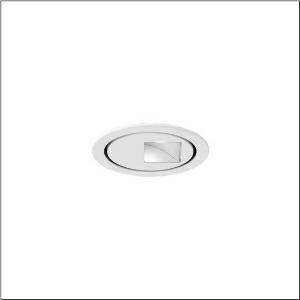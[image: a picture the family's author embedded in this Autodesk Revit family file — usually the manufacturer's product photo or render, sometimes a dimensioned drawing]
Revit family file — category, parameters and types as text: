
# Revit family: lunis_11_micro_round_51dj11b71wm21
name_source: partatom
category: Lighting Fixtures
units: mm (PartAtom-declared; Revit-internal decimal feet)

## family parameters
Cut with Voids When Loaded = No
Host = Face
Light Source = No
Part Type = Normal
Room Calculation Point = No
Round Connector Dimension = Use Diameter
Shared = No

## types (1)
- Lunis 11 micro round (1 x LED 3000K / CRI = 90 (unbekannt), 1100 lm, 3000K)
    Apparent Load = 20 VA
    CIE Flux Codes = 42 75 96 100 100
    Color Rendering = 90
    Color Temperature = 3000K
    Default Elevation = 1800 mm
    Description = Lunis 11 micro round, downlight, light control with wallwasher, of highly reflective aluminium, highly specular, light emission: direct distribution, LED rated luminous flux: 1.100lm, light colour: 930, with terminal, 3-pole, mains connection: 220..230V, AC, 50/60Hz, LED module, of aluminium, highly specular, white, diameter: 114mm, clamping range: 1..40mm, recessing ring, of plastic, traffic white (RAL 9016), protection rating (complete): IP20, insulation class (complete): insulation class II (safety insulation), certification: CE, permissible ambient temperature for indoor applications: 0..+35°C, packaging unit: 1 piece
    Height = 0 mm  [stored 0 ft]
    Lamp = 1 x LED 3000K / CRI >= 90 (unbekannt)
    Lamp Light Flux = 1100 lm
    Lamp count = 1
    Length = 114 mm
    Luminous efficacy = 56 lm/W
    Manufacturer = Siteco
    ModVariant = No
    Model = 51DJ11B71WM21
    Mounting Place = Ceiling
    Mounting Type = Recessed
    Number of Poles = 1
    OnlyDefault = Yes
    Power Factor = 1
    Product Name = Lunis 11 micro round
    Product group = downlight
    ProductGroupID = 401
    Protection Class = Protection class II
    Protection Degree = IP 20
    RLX_Detail_Level = 1
    RLX_Emergency_Light_Flux = 0 lm
    RLX_Emergency_Type = 0
    RLX_Emergency_Type_DB = No
    RlxData = <blob elided: 40609 chars, md5=cd65f293>
    Socket = socket
    Standby Power = 0 W
    System Light Flux = 1100 lm
    System Power = 20 W
    Type Comments = Product without accessories
    Type Image = l_1004773.jpg
    URL = http://relux.com
    VarID = ---
    Voltage = 0 V
    Weight = 0.00 kg
    Width = 114 mm

note: [stored X ft] marks values corroborated as IEEE doubles in the binary element streams (Revit-internal decimal feet)

## geometry (parser evidence)
native form markers: Blend x4, Sweep x12
no freeform markers — native parametric forms only
